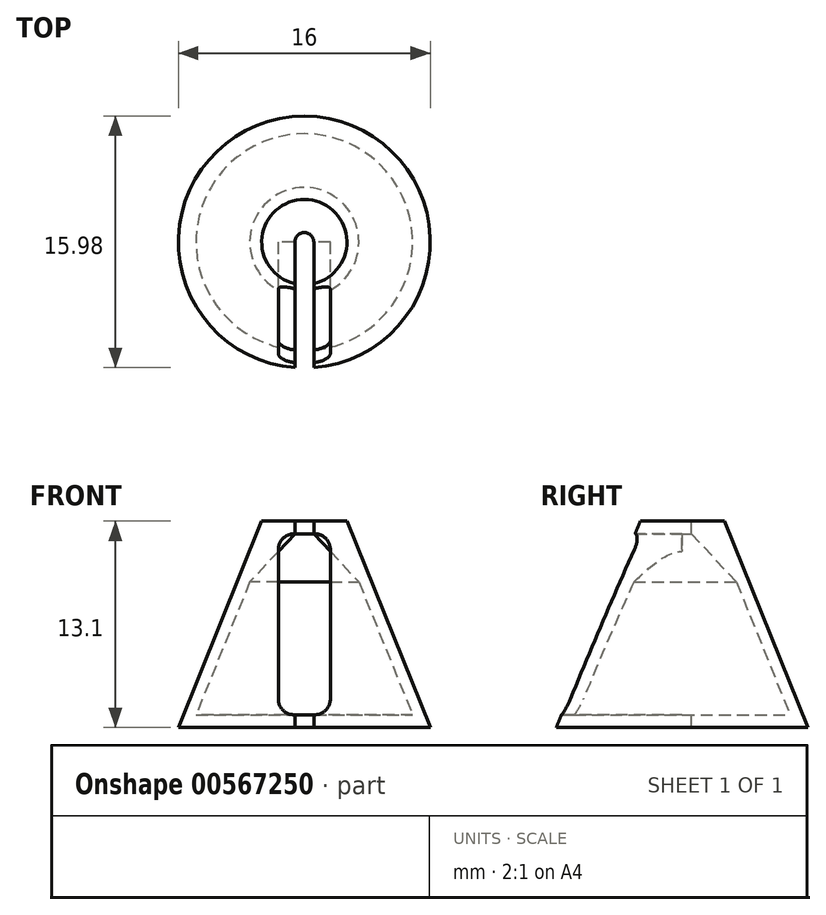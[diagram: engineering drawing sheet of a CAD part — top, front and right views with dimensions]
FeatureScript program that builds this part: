
annotation { "Feature Type Name" : "Feature", "Feature Type Description" : "" }
export const myFeature = defineFeature(function(context is Context, id is Id, definition is map)
    precondition{}
    {
        {
            assignVariable(context, id + "F0", {"name" : "disk_height", "anyValue" : 0.8});
        }
        {
            assignVariable(context, id + "F1", {"name" : "height", "anyValue" : 4 * 4 - 3.2 + 0.3});
        }
        {
            assignVariable(context, id + "F2", {"name" : "draft", "anyValue" : 22});
        }
        {
            assignVariable(context, id + "F3", {"name" : "voffset", "anyValue" : 0});
        }
        {
            var Q0;
            Q0=qCreatedBy(makeId("Top.planeOp"),FACE);
            var sketch = newSketch(context, id + "F4", { "sketchPlane" : qUnion([Q0])});
            skCircle(sketch, "E0", {"center": v(0, 0) * mm, "radius": 8 * mm});
            skCircle(sketch, "E1", {"center": v(0, 0) * mm, "radius": 7.2 * mm});
            skSolve(sketch);
        }
        {
            var Q0;
            Q0=makeQuery(id+"F4.imprint","IMPRINT",FACE,{"disambiguationData":[TD([[makeQuery(id+"F4.imprint","IMPRINT",EDGE,{"derivedFrom":sQuery(id+"F4.wireOp",EDGE,"ibTBWXkx-Vu6W-RPCG-L2gP-sItrhCC4QchF")}),1.0]])]});
            var Q1;
            Q1=makeQuery(id+"F4.imprint","IMPRINT",FACE,{"disambiguationData":[TD([[makeQuery(id+"F4.imprint","IMPRINT",EDGE,{"derivedFrom":sQuery(id+"F4.wireOp",EDGE,"E0")}),1.0]])]});
            var Q2;
            Q2=makeQuery(id+"F4.imprint","IMPRINT",FACE,{"disambiguationData":[TD([[makeQuery(id+"F4.imprint","IMPRINT",EDGE,{"derivedFrom":sQuery(id+"F4.wireOp",EDGE,"SsdXX7ms-AmTX-YumW-dS2f-ufH2UU8qdWA2")}),1.0]])]});
            var Q3;
            Q3=makeQuery(id+"F4.imprint","IMPRINT",FACE,{"disambiguationData":[TD([[makeQuery(id+"F4.imprint","IMPRINT",EDGE,{"derivedFrom":sQuery(id+"F4.wireOp",EDGE,"SsdXX7ms-AmTX-YumW-dS2f-ufH2UU8qdWA2")}),-1.0]])]});
            var Q4;
            Q4=makeQuery(id+"F4.imprint","IMPRINT",FACE,{"disambiguationData":[TD([[makeQuery(id+"F4.imprint","IMPRINT",EDGE,{"derivedFrom":sQuery(id+"F4.wireOp",EDGE,"E1")}),1.0]])]});
            extrude(context, id + "F5", {"entities" : qUnion([Q0, Q1, Q2, Q3, Q4]), "depth" : (getVariable(context, 'height') + getVariable(context, 'voffset')) * mm, "offsetDistance" : 25 * mm, "hasDraft" : true, "draftAngle" : (getVariable(context, 'draft')) * degree, "draftPullDirection" : true, "hasSecondDirection" : true, "secondDirectionOppositeDirection" : false, "secondDirectionDepth" : (getVariable(context, 'voffset')) * mm});
        }
        {
            var Q0;
            Q0=makeQuery(id+"F4.imprint","IMPRINT",FACE,{"disambiguationData":[TD([[makeQuery(id+"F4.imprint","IMPRINT",EDGE,{"derivedFrom":sQuery(id+"F4.wireOp",EDGE,"E1")}),1.0]])]});
            extrude(context, id + "F6", {"entities" : qUnion([Q0]), "operationType" : NewBodyOperationType.REMOVE, "depth" : (getVariable(context, 'height') - getVariable(context, 'disk_height')) * mm, "offsetDistance" : 25 * mm, "hasDraft" : true, "draftAngle" : (getVariable(context, 'draft')) * degree, "draftPullDirection" : true, "hasSecondDirection" : true, "secondDirectionOppositeDirection" : false, "secondDirectionDepth" : (getVariable(context, 'disk_height')) * mm});
        }
        {
            var Q0;
            Q0 = qSketchRegion(id + "F4", true);
            var Q1;
            Q1=makeQuery(id+"F4.imprint","IMPRINT",FACE,{"disambiguationData":[TD([[makeQuery(id+"F4.imprint","IMPRINT",EDGE,{"derivedFrom":sQuery(id+"F4.wireOp",EDGE,"E1")}),1.0]])]});
            extrude(context, id + "F7", {"entities" : qUnion([Q0, Q1]), "operationType" : NewBodyOperationType.ADD, "depth" : (getVariable(context, 'disk_height')) * mm, "offsetDistance" : 25 * mm, "hasDraft" : true, "draftAngle" : (getVariable(context, 'draft')) * degree, "draftPullDirection" : true});
        }
        {
            var Q0;
            Q0=makeQuery(id+"F5.opExtrude","CAP_FACE",FACE,{"disambiguationData":[OSD([sQuery(id+"F4.wireOp",EDGE,"E0")])],"isStart":false});
            var sketch = newSketch(context, id + "F8", { "sketchPlane" : qUnion([Q0])});
            skCircle(sketch, "E2", {"center": v(0, 0) * mm, "radius": 0.6 * mm});
            skLineSegment(sketch, "E3", {"start": v(0.6, 0) * mm, "end": v(0.6, -15.73) * mm});
            skLineSegment(sketch, "E4", {"start": v(-0.6, 0) * mm, "end": v(-0.6, -15.73) * mm});
            skLineSegment(sketch, "E5", {"start": v(-0.6, -15.73) * mm, "end": v(0.6, -15.73) * mm});
            skSolve(sketch);
        }
        {
            var Q0;
            Q0 = qSketchRegion(id + "F8", true);
            extrude(context, id + "F9", {"entities" : qUnion([Q0]), "operationType" : NewBodyOperationType.REMOVE, "endBound" : BoundingType.THROUGH_ALL, "oppositeDirection" : true, "depth" : 999 * mm, "offsetDistance" : 25 * mm});
        }
        {
            var Q0;
            Q0=qCreatedBy(makeId("Front.planeOp"),FACE);
            var sketch = newSketch(context, id + "F10", { "sketchPlane" : qUnion([Q0])});
            skPoint(sketch, "E6.0", {"position": v(0, 12.3) * mm});
            skPoint(sketch, "E7.0", {"position": v(0, 0.8) * mm});
            skLineSegment(sketch, "E8", {"start": v(0, 14.4) * mm, "end": v(0, -1.98) * mm, "construction": true});
            skCircle(sketch, "E9", {"center": v(0, 2.6) * mm, "radius": 1.6 * mm});
            skCircle(sketch, "E10", {"center": v(0, 4.6) * mm, "radius": 0.4 * mm});
            skCircle(sketch, "E11.1.0.0", {"center": v(0, 6.6) * mm, "radius": 1.6 * mm});
            skCircle(sketch, "E11.1.0.1", {"center": v(0, 8.6) * mm, "radius": 0.4 * mm});
            skCircle(sketch, "E11.2.0.0", {"center": v(0, 10.6) * mm, "radius": 1.6 * mm});
            skCircle(sketch, "E11.2.0.1", {"center": v(0, 12.6) * mm, "radius": 0.4 * mm});
            skLineSegment(sketch, "E11.direction1", {"start": v(0, 2.6) * mm, "end": v(0, 6.6) * mm, "construction": true});
            skLineSegment(sketch, "E12.0.2", {"start": v(6.88, 0.8) * mm, "end": v(-6.88, 0.8) * mm});
            skLineSegment(sketch, "E13.0.0", {"start": v(0.6, 12.3) * mm, "end": v(0.6, 13.1) * mm});
            skLineSegment(sketch, "E13.0.1", {"start": v(-0.6, 13.1) * mm, "end": v(0.6, 13.1) * mm});
            skLineSegment(sketch, "E13.0.2", {"start": v(-0.6, 13.1) * mm, "end": v(-0.6, 12.3) * mm});
            skLineSegment(sketch, "E13.0.3", {"start": v(0.6, 12.3) * mm, "end": v(-0.6, 12.3) * mm});
            skLineSegment(sketch, "E14", {"start": v(-2.23, 12.3) * mm, "end": v(-6.88, 0.8) * mm});
            skLineSegment(sketch, "E15", {"start": v(-0.6, 12.3) * mm, "end": v(-3.47, 9.24) * mm});
            skLineSegment(sketch, "E16", {"start": v(-2.23, 12.3) * mm, "end": v(-0.6, 12.3) * mm});
            skSolve(sketch);
        }
        {
            var Q0;
            {var subQ0=sQuery(id+"F10.wireOp",EDGE,"E16");Q0=makeQuery(id+"F10.imprint","IMPRINT",FACE,{"disambiguationData":[TD([[makeQuery(id+"F10.imprint","IMPRINT",EDGE,{"derivedFrom":subQ0}),-1.0]])]});}
            var Q1;
            Q1=sQuery(id+"F10.wireOp",EDGE,"E8");
            revolve(context, id + "F11", {"operationType" : NewBodyOperationType.ADD, "entities" : qUnion([Q0]), "axis" : qUnion([Q1]), "revolveType" : RevolveType.FULL});
        }
        {
            var Q0;
            Q0=qCreatedBy(makeId("Front.planeOp"),FACE);
            var sketch = newSketch(context, id + "F12", { "sketchPlane" : qUnion([Q0])});
            skLineSegment(sketch, "E17", {"start": v(-6.37, 2.04) * mm, "end": v(-2.23, 12.3) * mm});
            skLineSegment(sketch, "E18", {"start": v(2.23, 12.3) * mm, "end": v(6.88, 0.8) * mm});
            skLineSegment(sketch, "E19.bottom", {"start": v(1.65, 12.3) * mm, "end": v(-1.65, 12.3) * mm});
            skLineSegment(sketch, "E19.top", {"start": v(1.65, 0.8) * mm, "end": v(-1.65, 0.8) * mm});
            skLineSegment(sketch, "E19.left", {"start": v(1.65, 12.3) * mm, "end": v(1.65, 0.8) * mm});
            skLineSegment(sketch, "E19.right", {"start": v(-1.65, 12.3) * mm, "end": v(-1.65, 0.8) * mm});
            skPoint(sketch, "E19.middle", {"position": v(0, 6.55) * mm});
            skPoint(sketch, "E19.middle.positionSnap0", {"position": v(4.55, 6.55) * mm});
            skPoint(sketch, "E19.centerSnap0", {"position": v(4.55, 6.55) * mm});
            skSolve(sketch);
        }
        {
            var Q0;
            {var subQ7=sQuery(id+"F12.wireOp",EDGE,"E19.top");Q0=makeQuery(id+"F12.imprint","IMPRINT",FACE,{"disambiguationData":[TD([[makeQuery(id+"F12.imprint","IMPRINT",EDGE,{"derivedFrom":subQ7}),-1.0]])]});}
            var Q1;
            {var subQ0=sQuery(id+"F12.wireOp",EDGE,"E19.bottom");var subQ1=sQuery(id+"F12.wireOp",EDGE,"E18");var subQ2=makeQuery(id+"F12.imprint","INTERSECT",VERTEX,{"derivedFrom":[subQ1,subQ0]});Q1=makeQuery(id+"F12.imprint","IMPRINT",FACE,{"disambiguationData":[TD([[makeQuery(id+"F12.imprint","IMPRINT",EDGE,{"disambiguationData":[TD([[subQ2,-1.0]])],"derivedFrom":subQ1}),1.0]])]});}
            var Q2;
            {var subQ0=sQuery(id+"F12.wireOp",EDGE,"E19.bottom");var subQ1=sQuery(id+"F12.wireOp",EDGE,"E17");var subQ2=makeQuery(id+"F12.imprint","INTERSECT",VERTEX,{"derivedFrom":[subQ1,subQ0]});Q2=makeQuery(id+"F12.imprint","IMPRINT",FACE,{"disambiguationData":[TD([[makeQuery(id+"F12.imprint","IMPRINT",EDGE,{"disambiguationData":[TD([[subQ2,1.0]])],"derivedFrom":subQ1}),1.0]])]});}
            extrude(context, id + "F13", {"entities" : qUnion([Q0, Q1, Q2]), "operationType" : NewBodyOperationType.REMOVE, "endBound" : BoundingType.THROUGH_ALL, "depth" : 25 * mm, "offsetDistance" : 25 * mm});
        }
        {
            var Q0;
            Q0=makeQuery(id+"F13.boolean.opBoolean","COPY",EDGE,{"derivedFrom":makeQuery(id+"F13.opExtrude","SWEPT_EDGE",EDGE,{"disambiguationData":[OSD([sQuery(id+"F12.wireOp",EDGE,"E19.bottom"),sQuery(id+"F12.wireOp",EDGE,"E19.left")])]})});
            var Q1;
            Q1=makeQuery(id+"F13.boolean.opBoolean","COPY",EDGE,{"derivedFrom":makeQuery(id+"F13.opExtrude","SWEPT_EDGE",EDGE,{"disambiguationData":[OSD([sQuery(id+"F12.wireOp",EDGE,"E19.bottom"),sQuery(id+"F12.wireOp",EDGE,"E19.right")])]})});
            fillet(context, id + "F14", {"entities" : qUnion([Q0, Q1]), "radius" : 1 * mm, "tangentPropagation" : true, "allowEdgeOverflow" : false});
        }
        {
            var Q0;
            Q0=makeQuery(id+"F13.boolean.opBoolean","COPY",EDGE,{"derivedFrom":makeQuery(id+"F13.opExtrude","SWEPT_EDGE",EDGE,{"disambiguationData":[OSD([sQuery(id+"F12.wireOp",EDGE,"E19.top"),sQuery(id+"F12.wireOp",EDGE,"E19.left")])]})});
            var Q1;
            Q1=makeQuery(id+"F13.boolean.opBoolean","COPY",EDGE,{"derivedFrom":makeQuery(id+"F13.opExtrude","SWEPT_EDGE",EDGE,{"disambiguationData":[OSD([sQuery(id+"F12.wireOp",EDGE,"E19.top"),sQuery(id+"F12.wireOp",EDGE,"E19.right")])]})});
            fillet(context, id + "F15", {"entities" : qUnion([Q0, Q1]), "radius" : 1 * mm, "tangentPropagation" : true, "allowEdgeOverflow" : false});
        }
    });
